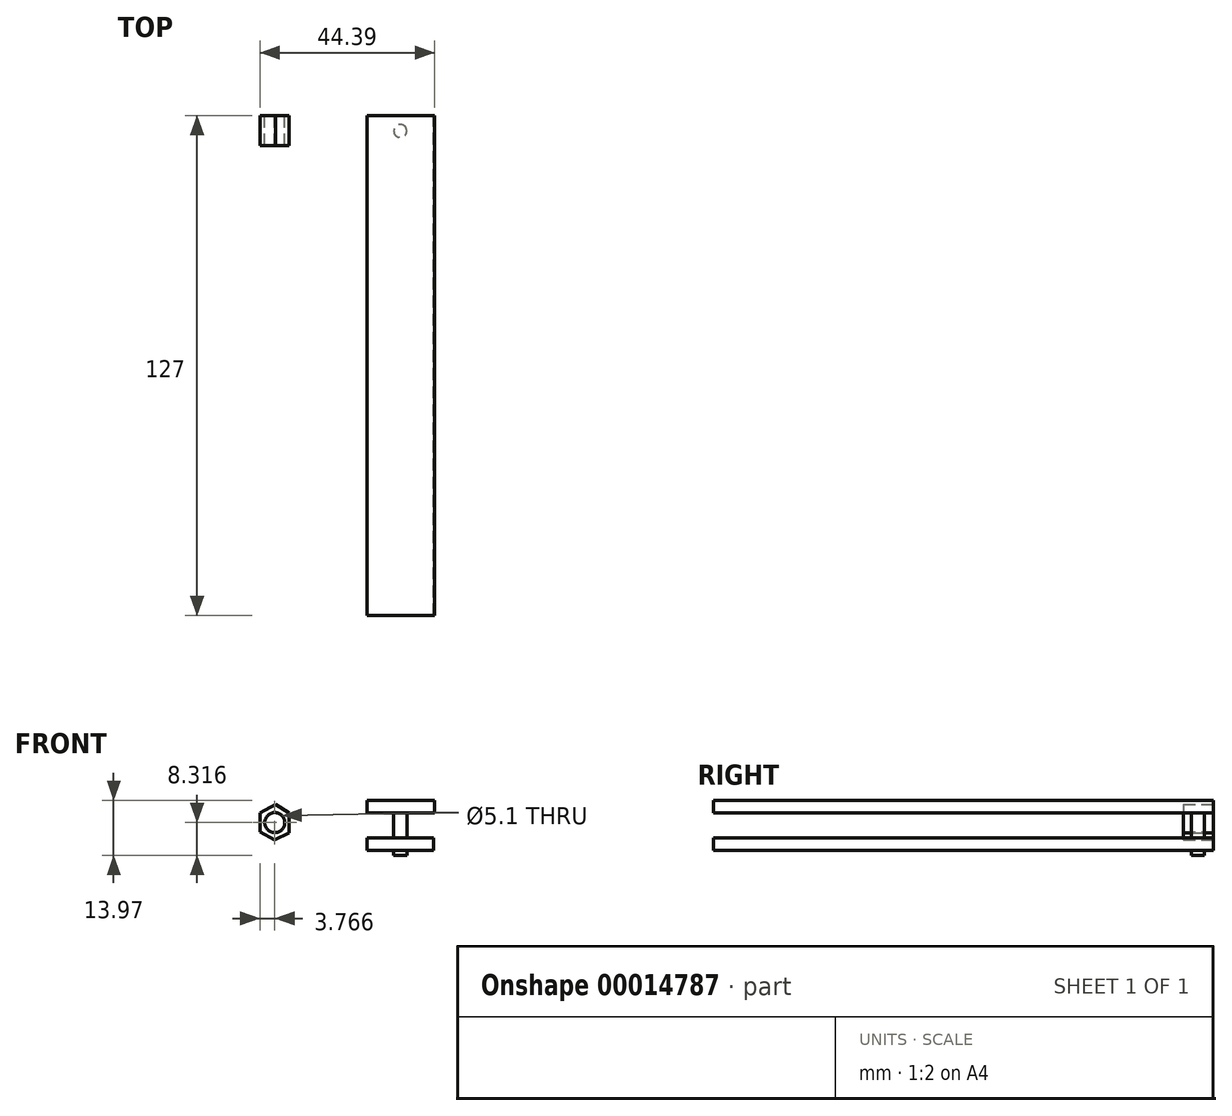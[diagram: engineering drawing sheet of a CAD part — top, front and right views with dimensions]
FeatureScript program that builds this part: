
annotation { "Feature Type Name" : "Feature", "Feature Type Description" : "" }
export const myFeature = defineFeature(function(context is Context, id is Id, definition is map)
    precondition{}
    {
        {
            var Q0;
            Q0=qCreatedBy(makeId("Front.planeOp"),FACE);
            var sketch = newSketch(context, id + "F0", { "sketchPlane" : qUnion([Q0])});
            skLineSegment(sketch, "E0.bottom", {"start": v(0, 0) * mm, "end": v(17.15, 0) * mm});
            skLineSegment(sketch, "E0.top", {"start": v(0, 3.18) * mm, "end": v(17.15, 3.18) * mm});
            skLineSegment(sketch, "E0.left", {"start": v(0, 0) * mm, "end": v(0, 3.18) * mm});
            skLineSegment(sketch, "E0.right", {"start": v(17.15, 0) * mm, "end": v(17.15, 3.18) * mm});
            skLineSegment(sketch, "E1.bottom", {"start": v(0, -6.35) * mm, "end": v(16.9, -6.35) * mm});
            skLineSegment(sketch, "E1.top", {"start": v(0, -9.52) * mm, "end": v(16.9, -9.52) * mm});
            skLineSegment(sketch, "E1.left", {"start": v(0, -6.35) * mm, "end": v(0, -9.52) * mm});
            skLineSegment(sketch, "E1.right", {"start": v(16.9, -6.35) * mm, "end": v(16.9, -9.52) * mm});
            skLineSegment(sketch, "E2.bottom", {"start": v(17.15, 0) * mm, "end": v(17.01, 0) * mm});
            skLineSegment(sketch, "E2.top", {"start": v(17.04, -6.35) * mm, "end": v(16.9, -6.35) * mm});
            skSolve(sketch);
        }
        {
            var Q0;
            Q0 = qSketchRegion(id + "F0", true);
            extrude(context, id + "F1", {"entities" : qUnion([Q0]), "depth" : 127 * mm});
        }
        {
            var Q0;
            Q0=qCreatedBy(makeId("Front.planeOp"),FACE);
            var sketch = newSketch(context, id + "F2", { "sketchPlane" : qUnion([Q0])});
            skLineSegment(sketch, "E3", {"start": v(-27.25, 0) * mm, "end": v(-27.25, -4.9) * mm});
            skLineSegment(sketch, "E4", {"start": v(-27.25, -4.9) * mm, "end": v(-23.48, -6.85) * mm});
            skLineSegment(sketch, "E5", {"start": v(-23.48, -6.85) * mm, "end": v(-19.87, -5.04) * mm});
            skLineSegment(sketch, "E6", {"start": v(-19.87, -5.04) * mm, "end": v(-19.87, 0) * mm});
            skLineSegment(sketch, "E7", {"start": v(-19.87, 0) * mm, "end": v(-23.33, 2.18) * mm});
            skLineSegment(sketch, "E8", {"start": v(-23.33, 2.18) * mm, "end": v(-27.25, 0) * mm});
            skCircle(sketch, "E9", {"center": v(-23.48, -2.48) * mm, "radius": 2.55 * mm});
            skSolve(sketch);
        }
        {
            var Q0;
            Q0=makeQuery(id+"F2.imprint","IMPRINT",FACE,{"disambiguationData":[TD([[makeQuery(id+"F2.imprint","IMPRINT",EDGE,{"derivedFrom":sQuery(id+"F2.wireOp",EDGE,"E3")}),1.0]])]});
            extrude(context, id + "F3", {"entities" : qUnion([Q0]), "depth" : 7.62 * mm});
        }
        {
            var Q0;
            Q0=makeQuery(id+"F1.opExtrude","SWEPT_FACE",FACE,{"disambiguationData":[OSD([sQuery(id+"F0.wireOp",EDGE,"E0.top")])]});
            var sketch = newSketch(context, id + "F4", { "sketchPlane" : qUnion([Q0])});
            skCircle(sketch, "E10", {"center": v(8.4, -3.91) * mm, "radius": 1.65 * mm});
            skSolve(sketch);
        }
        {
            var Q0;
            Q0 = qSketchRegion(id + "F4", true);
            extrude(context, id + "F5", {"entities" : qUnion([Q0]), "operationType" : NewBodyOperationType.ADD, "oppositeDirection" : true, "depth" : 13.97 * mm});
        }
    });
